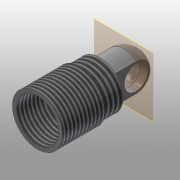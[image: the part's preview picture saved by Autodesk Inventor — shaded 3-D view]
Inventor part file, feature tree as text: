
AUTODESK INVENTOR PART (.ipt)
format: ipt  version: 2016 (Build 200138000, 138)  size: 166,400 bytes
history: native  units: mm
features: sketch x6, extrude x3, revolve x2, hole x2, thread x2, plane x1, other x1
ambient origin geometry x8: Origin, YZ Plane, XZ Plane, XY Plane, X Axis, Y Axis, Z Axis, Center Point
bodies: Solid1 (feature_tree)
feature tree (17):
  extrude  "Extrusion1"  Depth=11.0mm TaperAngle=0.0deg
  extrude  "Extrusion2"  Depth=5.0mm TaperAngle=0.0deg
  revolve  "Revolution1"  Angle=90.0deg
  extrude  "Extrusion3"  Depth=5.0mm TaperAngle=0.0deg
  hole  "Hole1"  [1 undecoded]
  thread  "Thread1"  [1 undecoded]
  thread  "Thread2"  [1 undecoded]
  hole  "Hole2"  [1 undecoded]
  plane  "Work Plane1"
  revolve  "Revolution2"  [1 undecoded]
  sketch  "Sketch1"  dims[d0=12.917mm d1=11.0mm d2=0.0mm]
  sketch  "Sketch2"  dims[d3=12.0mm d4=5.0mm d5=0.0mm]
  sketch  "Sketch3"  dims[d7=4.8mm d8=90.0deg]
  sketch  "Sketch4"  dims[d9=5.0mm d10=13.25mm d11=0.0mm]
  sketch  "Sketch5"  dims[d13=22.2mm d14=10.0mm d15=10.0mm]
  other  "Work Axis1"
  sketch  "Sketch6"  dims[d16=6.1mm d17=6.0mm d18=4.0mm d19=2.0mm d20=90.0deg d21=8.0mm d22=20.594885mm d23=10.0mm d24=0.0mm d25=10.0mm d26=0.0mm d27=12.0mm d28=10.917mm d29=8.5mm d30=4.0mm d31=2.0mm d32=90.0deg d33=10.0mm d34=0.0mm d35=0.0mm d36=6.6mm d37=90.0deg]
note: 5 required parameter values undecoded (feature->parameter linkage not recoverable at this tier; creation-order binding heuristic only, values carry confidence <= 0.55)